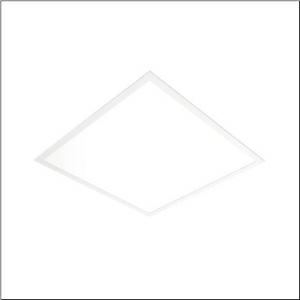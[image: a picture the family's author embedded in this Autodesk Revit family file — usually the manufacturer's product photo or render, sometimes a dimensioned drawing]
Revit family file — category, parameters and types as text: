
# Revit family: apollon_r__41_51mh12h72443_9ce2
name_source: partatom
category: Lighting Fixtures
units: mm (PartAtom-declared; Revit-internal decimal feet)

## family parameters
Cut with Voids When Loaded = No
Host = Face
Light Source = No
Part Type = Normal
Room Calculation Point = No
Round Connector Dimension = Use Diameter
Shared = No

## types (1)
- Apollon® 41 (1 x LED, 5000 lm, 38.5 W, 4000K)
    Apparent Load = 39 VA
    CIE Flux Codes = 61 87 97 100 100
    Color Rendering = 80
    Color Temperature = 4000K
    Default Elevation = 1800 mm
    Description = Apollon® 41, office luminaire, primary optical cover: prismatic diffuser, of PS, light emission: direct distribution, primary light characteristic: symmetric, installation type: lay-in mounting, LED, rated luminous flux: 5.000lm, luminous efficacy: 130lm/W, light colour: 840, colour temperature: 4000K, control gear: ON/OFF, with terminal, 3-pole, mains connection: 220..240V, AC, 50/60Hz, rated input power: 38.5W, housing, of aluminium section, traffic white (RAL 9016), module: M600, length: 595mm, width: 595mm, height: 60mm, recess depth: 180mm, housing upper side, of sheet steel, protection rating (complete): IP20, protection rating (lamp compartment, on room side): IP40, insulation class (complete): insulation class II (safety insulation), certification: CE, ENEC, impact resistance: IK03, permissible operating ambient temperature: -25..+40°C, packaging unit: 1 piece
    Height = 0 mm  [stored 0 ft]
    Lamp = 1 x LED
    Lamp Light Flux = 5000 lm
    Lamp Power = 38.5 W
    Lamp count = 1
    Length = 600 mm
    Luminous efficacy = 130 lm/W
    Manufacturer = Siteco
    ModVariant = No
    Model = 51MH12H72443
    Mounting Place = Ceiling
    Mounting Type = Recessed
    Number of Poles = 1
    OnlyDefault = Yes
    Power Factor = 1
    Product Name = Apollon® 41
    Product group = office luminaire | ceiling recessed
    ProductGroupID = 401
    Protection Class = Protection class II
    Protection Degree = IP 20
    RLX_Detail_Level = 1
    RLX_Emergency_Light_Flux = 0 lm
    RLX_Emergency_Type = 0
    RLX_Emergency_Type_DB = No
    RlxData = <blob elided: 12285 chars, md5=89143d48>
    Socket = socket
    Standby Power = 0 W
    System Light Flux = 5000 lm
    System Power = 39 W
    Type Comments = Product without accessories
    Type Image = l_1291024.jpg
    URL = http://relux.com
    VarID = ---
    Voltage = 0 V
    Weight = 0.00 kg
    Width = 600 mm

note: [stored X ft] marks values corroborated as IEEE doubles in the binary element streams (Revit-internal decimal feet)

## geometry (parser evidence)
native form markers: Sweep x9
no freeform markers — native parametric forms only
